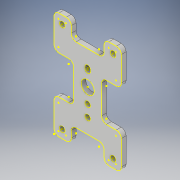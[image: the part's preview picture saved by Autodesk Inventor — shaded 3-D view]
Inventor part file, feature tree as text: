
AUTODESK INVENTOR PART (.ipt)
format: ipt  version: 2019 (Build 230136000, 136)  size: 241,152 bytes
history: native  units: mm
features: sketch x4, extrude x2, hole x1, fillet x1, projected_geometry x1
ambient origin geometry x8: Origin, YZ Plane, XZ Plane, XY Plane, X Axis, Y Axis, Z Axis, Center Point
bodies: Solid1 (feature_tree)
feature tree (9):
  sketch  "Sketch1"  dims[d0=41.0mm d1=65.3mm d2=21.0mm d3=21.0mm d4=12.0mm d5=9.0mm d6=9.0mm d7=7.0mm d8=1.0mm d9=5.0mm d11=5.0mm d12=41.0mm d13=41.0mm d14=12.0mm d15=10.5mm d16=10.5mm d17=8.0mm d18=20.5mm d19=5.0mm]
  extrude  "Extrusion1"  Depth=10.5mm
  hole  "Hole1"  [1 undecoded]
  fillet  "Fillet1"  Radius=3.0mm
  extrude  "Extrusion2"  Depth=3.0mm TaperAngle=0.0deg
  sketch  "Sketch4"  dims[d43=3.3mm d44=6.0mm d45=4.0mm d46=2.0mm d47=90.0deg d48=8.0mm d49=20.594885mm d50=3.0mm d51=3.0mm d52=0.0mm]
  sketch  "Sketch2"  dims[d20=5.0mm]
  sketch  "Sketch3"  dims[d21=41.0mm d22=65.3mm d23=21.0mm d24=21.0mm d25=12.0mm d28=7.0mm d29=1.0mm d30=5.0mm d31=5.0mm d32=41.0mm d33=41.0mm d34=12.0mm d35=10.5mm d36=10.5mm d37=8.0mm d38=20.5mm d39=5.0mm d40=5.0mm d41=3.0mm d42=0.0mm]
  projected_geometry  "Projected Loop1"
note: 1 required parameter value undecoded (feature->parameter linkage not recoverable at this tier; creation-order binding heuristic only, values carry confidence <= 0.55)
